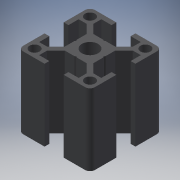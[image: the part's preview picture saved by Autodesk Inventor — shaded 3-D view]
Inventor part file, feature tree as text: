
AUTODESK INVENTOR PART (.ipt)
format: ipt  version: 2016 (Build 200138000, 138)  size: 201,728 bytes
history: native  units: mm
features: other x21, sketch x3, hole x2, extrude x1, pattern_linear x1
ambient origin geometry x8: Origin, YZ Plane, XZ Plane, XY Plane, X Axis, Y Axis, Z Axis, Center Point
bodies: Solid1 (feature_tree)
feature tree (28):
  extrude  "Extrusion1"  Depth=2.0mm
  hole  "Hole1"  [1 undecoded]
  hole  "Hole2"  [1 undecoded]
  pattern_linear  "Rectangular Pattern1"  Spacing1=0.0mm  [1 undecoded]
  other  "C1_XY"
  other  "C1_YZ"
  other  "C1_ZX"
  other  "C1_X"
  other  "C1_Y"
  other  "C1_Z"
  other  "C1_Center"
  other  "to_frame_cap1_XY"
  other  "to_frame_cap1_YZ"
  other  "to_frame_cap1_ZX"
  other  "to_frame_cap1_X"
  other  "to_frame_cap1_Y"
  other  "to_frame_cap1_Z"
  other  "to_frame_cap1_Center"
  other  "to_frame_cap2_XY"
  other  "to_frame_cap2_YZ"
  other  "to_frame_cap2_ZX"
  other  "to_frame_cap2_X"
  other  "to_frame_cap2_Y"
  other  "to_frame_cap2_Z"
  other  "to_frame_cap2_Center"
  sketch  "Sketch_1"  dims[d0=30.0mm d1=0.0mm]
  sketch  "Sketch2"  dims[d2=6.8mm d3=6.0mm d4=4.0mm d5=2.0mm d6=90.0deg d7=140.0mm d8=0.0mm]
  sketch  "Sketch3"  dims[d9=4.2mm d10=6.0mm d11=4.0mm d12=2.0mm d13=90.0deg d14=140.0mm d15=0.0mm d16=20.0mm d18=23.2mm d19=20.0mm d21=23.2mm d22=0.0mm d23=0.0mm d24=0.0mm]
note: 3 required parameter values undecoded (feature->parameter linkage not recoverable at this tier; creation-order binding heuristic only, values carry confidence <= 0.55)
